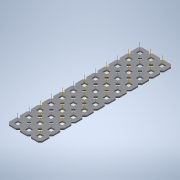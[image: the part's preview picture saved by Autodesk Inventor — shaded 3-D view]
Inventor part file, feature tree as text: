
AUTODESK INVENTOR PART (.ipt)
format: ipt  version: 2020 (Build 240168000, 168)  size: 1,136,128 bytes
history: native  units: in
note: dims shown in document units (in); Inventor stores cm internally (conversion verified against a paired STEP export)
features: other x45, extrude x2, plane x2, split x2, pattern_linear x1, imported_body x1
ambient origin geometry x8: Origin, YZ Plane, XZ Plane, XY Plane, X Axis, Y Axis, Z Axis, Center Point
bodies: Body1 (feature_tree)
feature tree (53):
  other  "Diamond-Pattern"
  other  "Plate"
  extrude  "length cut"  TaperAngle=0.0deg  [1 undecoded]
  extrude  "width cut"  TaperAngle=0.0deg  [1 undecoded]
  other  "constraint axis"
  pattern_linear  "constraint axes"  Spacing1=0.5in  [1 undecoded]
  other  "front plane"
  other  "right plane"
  plane  "Work Plane5"
  split  "Split1"
  plane  "Work Plane6"
  split  "Split2"
  imported_body  "Base1"
  other  "length profile"
  other  "width profile"
  other  "Work Point1"
  other  "Work Axis36"
  other  "Work Axis37"
  other  "Work Axis38"
  other  "Work Axis39"
  other  "Work Axis40"
  other  "Work Axis41"
  other  "Work Axis42"
  other  "Work Axis43"
  other  "Work Axis44"
  other  "Work Axis45"
  other  "Work Axis46"
  other  "Work Axis47"
  other  "Work Axis48"
  other  "Work Axis49"
  other  "Work Axis50"
  other  "Work Axis51"
  other  "Work Axis52"
  other  "Work Axis53"
  other  "Work Axis54"
  other  "Work Axis55"
  other  "Work Axis56"
  other  "Work Axis57"
  other  "Work Axis58"
  other  "Work Axis59"
  other  "Work Axis60"
  other  "Work Axis61"
  other  "Work Axis62"
  other  "Work Axis63"
  other  "Work Axis64"
  other  "back plane"
  other  "left plane"
  other  "Work Axis75"
  other  "Work Axis76"
  other  "Work Axis77"
  other  "Work Axis78"
  other  "Work Axis79"
  other  "Work Axis80"
note: 3 required parameter values undecoded (feature->parameter linkage not recoverable at this tier; creation-order binding heuristic only, values carry confidence <= 0.55)
